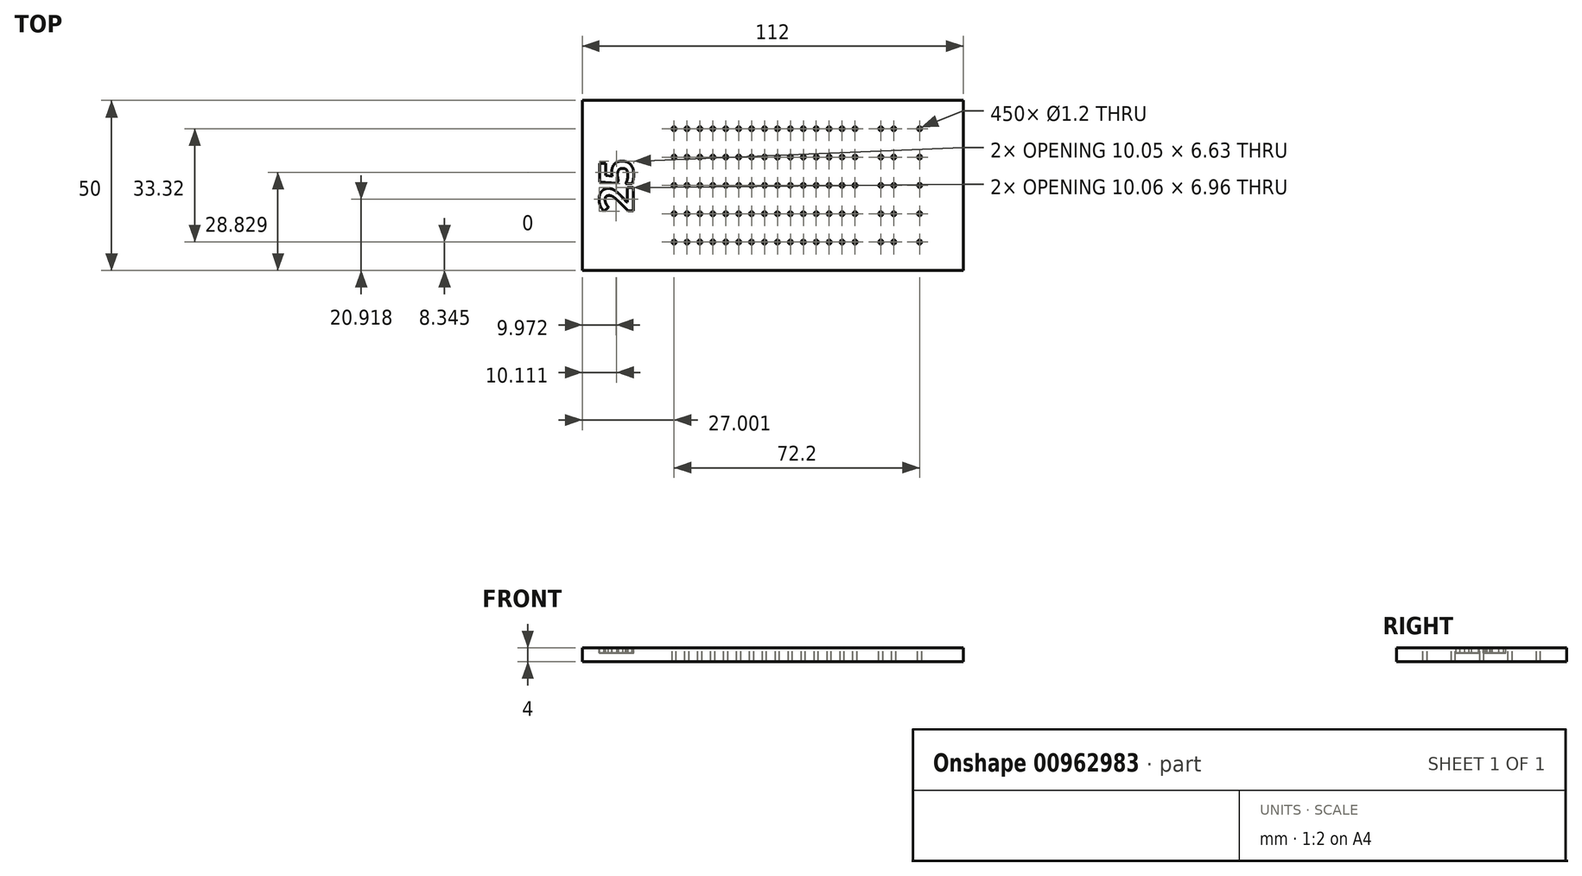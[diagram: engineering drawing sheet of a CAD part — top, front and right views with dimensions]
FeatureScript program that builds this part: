
annotation { "Feature Type Name" : "Feature", "Feature Type Description" : "" }
export const myFeature = defineFeature(function(context is Context, id is Id, definition is map)
    precondition{}
    {
        {
            var Q0;
            Q0=qCreatedBy(makeId("Top.planeOp"),FACE);
            var sketch = newSketch(context, id + "F0", { "sketchPlane" : qUnion([Q0])});
            skLineSegment(sketch, "E0.bottom", {"start": v(-43.16, 28.34) * mm, "end": v(68.84, 28.34) * mm});
            skLineSegment(sketch, "E0.top", {"start": v(-43.16, -21.66) * mm, "end": v(68.84, -21.66) * mm});
            skLineSegment(sketch, "E0.left", {"start": v(-43.16, 28.34) * mm, "end": v(-43.16, -21.66) * mm});
            skLineSegment(sketch, "E0.right", {"start": v(68.84, 28.34) * mm, "end": v(68.84, -21.66) * mm});
            skSolve(sketch);
        }
        {
            var Q0;
            Q0=makeQuery(id+"F0.imprint","IMPRINT",FACE,{"disambiguationData":[TD([[makeQuery(id+"F0.imprint","IMPRINT",EDGE,{"derivedFrom":sQuery(id+"F0.wireOp",EDGE,"E0.bottom")}),-1.0]])]});
            extrude(context, id + "F1", {"entities" : qUnion([Q0]), "depth" : 4 * mm, "offsetDistance" : 25 * mm});
        }
        {
            var Q0;
            Q0=makeQuery(id+"F1.opExtrude","CAP_FACE",FACE,{"disambiguationData":[OSD([sQuery(id+"F0.wireOp",EDGE,"E0.bottom"),sQuery(id+"F0.wireOp",EDGE,"E0.top"),sQuery(id+"F0.wireOp",EDGE,"E0.left"),sQuery(id+"F0.wireOp",EDGE,"E0.right")])],"isStart":false});
            var sketch = newSketch(context, id + "F2", { "sketchPlane" : qUnion([Q0])});
            skText(sketch, "E1", { "text": "25", "fontName": "OpenSans-Bold.ttf"});
            const initialGuessF2  = {"E1": [-0.02816, -0.00475, 0, 1, 0.01]};
            skSetInitialGuess(sketch, initialGuessF2);
            skSolve(sketch);
        }
        {
            var Q0;
            Q0=qSketchRegion(id+"F2",true);
            extrude(context, id + "F3", {"entities" : qUnion([Q0]), "operationType" : NewBodyOperationType.REMOVE, "oppositeDirection" : true, "depth" : 1.5 * mm, "offsetDistance" : 25 * mm});
        }
        {
            var Q0;
            {var subQ0=sQuery(id+"F0.wireOp",EDGE,"E0.left");var subQ1=sQuery(id+"F0.wireOp",EDGE,"E0.bottom");var subQ2=sQuery(id+"F0.wireOp",EDGE,"E0.right");var subQ3=sQuery(id+"F0.wireOp",EDGE,"E0.top");Q0=makeQuery(id+"F3.boolean.opBoolean","SPLIT",FACE,{"disambiguationData":[TD([makeQuery(id+"F1.opExtrude","SWEPT_FACE",FACE,{"disambiguationData":[OSD([subQ1])]})])],"derivedFrom":makeQuery(id+"F1.opExtrude","CAP_FACE",FACE,{"disambiguationData":[OSD([subQ1,subQ3,subQ0,subQ2])],"isStart":false})});}
            var sketch = newSketch(context, id + "F4", { "sketchPlane" : qUnion([Q0])});
            skCircle(sketch, "E2", {"center": v(-16.16, 20) * mm, "radius": 0.6 * mm});
            skCircle(sketch, "E3", {"center": v(-12.36, 20) * mm, "radius": 0.6 * mm});
            skCircle(sketch, "E4", {"center": v(-8.56, 20) * mm, "radius": 0.6 * mm});
            skCircle(sketch, "E5", {"center": v(-4.76, 20) * mm, "radius": 0.6 * mm});
            skCircle(sketch, "E6", {"center": v(-0.96, 20) * mm, "radius": 0.6 * mm});
            skCircle(sketch, "E7", {"center": v(2.84, 20) * mm, "radius": 0.6 * mm});
            skCircle(sketch, "E8", {"center": v(6.64, 20) * mm, "radius": 0.6 * mm});
            skCircle(sketch, "E9", {"center": v(10.44, 20) * mm, "radius": 0.6 * mm});
            skCircle(sketch, "E10", {"center": v(14.24, 20) * mm, "radius": 0.6 * mm});
            skCircle(sketch, "E11", {"center": v(18.04, 20) * mm, "radius": 0.6 * mm});
            skCircle(sketch, "E12", {"center": v(21.84, 20) * mm, "radius": 0.6 * mm});
            skCircle(sketch, "E13", {"center": v(25.64, 20) * mm, "radius": 0.6 * mm});
            skCircle(sketch, "E14", {"center": v(29.44, 20) * mm, "radius": 0.6 * mm});
            skCircle(sketch, "E15", {"center": v(33.24, 20) * mm, "radius": 0.6 * mm});
            skCircle(sketch, "E16", {"center": v(37.04, 20) * mm, "radius": 0.6 * mm});
            skCircle(sketch, "E17", {"center": v(44.64, 20) * mm, "radius": 0.6 * mm});
            skCircle(sketch, "E18", {"center": v(48.44, 20) * mm, "radius": 0.6 * mm});
            skCircle(sketch, "E19", {"center": v(56.04, 20) * mm, "radius": 0.6 * mm});
            skCircle(sketch, "E20", {"center": v(-16.16, 11.68) * mm, "radius": 0.6 * mm});
            skCircle(sketch, "E21", {"center": v(-12.36, 11.68) * mm, "radius": 0.6 * mm});
            skCircle(sketch, "E22", {"center": v(-8.56, 11.68) * mm, "radius": 0.6 * mm});
            skCircle(sketch, "E23", {"center": v(-4.76, 11.68) * mm, "radius": 0.6 * mm});
            skCircle(sketch, "E24", {"center": v(-0.96, 11.68) * mm, "radius": 0.6 * mm});
            skCircle(sketch, "E25", {"center": v(2.84, 11.68) * mm, "radius": 0.6 * mm});
            skCircle(sketch, "E26", {"center": v(6.64, 11.68) * mm, "radius": 0.6 * mm});
            skCircle(sketch, "E27", {"center": v(10.44, 11.68) * mm, "radius": 0.6 * mm});
            skCircle(sketch, "E28", {"center": v(14.24, 11.68) * mm, "radius": 0.6 * mm});
            skCircle(sketch, "E29", {"center": v(18.04, 11.68) * mm, "radius": 0.6 * mm});
            skCircle(sketch, "E30", {"center": v(21.84, 11.68) * mm, "radius": 0.6 * mm});
            skCircle(sketch, "E31", {"center": v(25.64, 11.68) * mm, "radius": 0.6 * mm});
            skCircle(sketch, "E32", {"center": v(29.44, 11.68) * mm, "radius": 0.6 * mm});
            skCircle(sketch, "E33", {"center": v(33.24, 11.68) * mm, "radius": 0.6 * mm});
            skCircle(sketch, "E34", {"center": v(37.04, 11.68) * mm, "radius": 0.6 * mm});
            skCircle(sketch, "E35", {"center": v(44.64, 11.68) * mm, "radius": 0.6 * mm});
            skCircle(sketch, "E36", {"center": v(48.44, 11.68) * mm, "radius": 0.6 * mm});
            skCircle(sketch, "E37", {"center": v(56.04, 11.68) * mm, "radius": 0.6 * mm});
            skCircle(sketch, "E38", {"center": v(-16.16, 3.35) * mm, "radius": 0.6 * mm});
            skCircle(sketch, "E39", {"center": v(-12.36, 3.35) * mm, "radius": 0.6 * mm});
            skCircle(sketch, "E40", {"center": v(-8.56, 3.35) * mm, "radius": 0.6 * mm});
            skCircle(sketch, "E41", {"center": v(-4.76, 3.35) * mm, "radius": 0.6 * mm});
            skCircle(sketch, "E42", {"center": v(-0.96, 3.35) * mm, "radius": 0.6 * mm});
            skCircle(sketch, "E43", {"center": v(2.84, 3.35) * mm, "radius": 0.6 * mm});
            skCircle(sketch, "E44", {"center": v(6.64, 3.35) * mm, "radius": 0.6 * mm});
            skCircle(sketch, "E45", {"center": v(10.44, 3.35) * mm, "radius": 0.6 * mm});
            skCircle(sketch, "E46", {"center": v(14.24, 3.35) * mm, "radius": 0.6 * mm});
            skCircle(sketch, "E47", {"center": v(18.04, 3.35) * mm, "radius": 0.6 * mm});
            skCircle(sketch, "E48", {"center": v(21.84, 3.35) * mm, "radius": 0.6 * mm});
            skCircle(sketch, "E49", {"center": v(25.64, 3.35) * mm, "radius": 0.6 * mm});
            skCircle(sketch, "E50", {"center": v(29.44, 3.35) * mm, "radius": 0.6 * mm});
            skCircle(sketch, "E51", {"center": v(33.24, 3.35) * mm, "radius": 0.6 * mm});
            skCircle(sketch, "E52", {"center": v(37.04, 3.35) * mm, "radius": 0.6 * mm});
            skCircle(sketch, "E53", {"center": v(44.64, 3.35) * mm, "radius": 0.6 * mm});
            skCircle(sketch, "E54", {"center": v(48.44, 3.35) * mm, "radius": 0.6 * mm});
            skCircle(sketch, "E55", {"center": v(56.04, 3.35) * mm, "radius": 0.6 * mm});
            skCircle(sketch, "E56", {"center": v(-16.16, -4.98) * mm, "radius": 0.6 * mm});
            skCircle(sketch, "E57", {"center": v(-12.36, -4.98) * mm, "radius": 0.6 * mm});
            skCircle(sketch, "E58", {"center": v(-8.56, -4.98) * mm, "radius": 0.6 * mm});
            skCircle(sketch, "E59", {"center": v(-4.76, -4.98) * mm, "radius": 0.6 * mm});
            skCircle(sketch, "E60", {"center": v(-0.96, -4.98) * mm, "radius": 0.6 * mm});
            skCircle(sketch, "E61", {"center": v(2.84, -4.98) * mm, "radius": 0.6 * mm});
            skCircle(sketch, "E62", {"center": v(6.64, -4.98) * mm, "radius": 0.6 * mm});
            skCircle(sketch, "E63", {"center": v(10.44, -4.98) * mm, "radius": 0.6 * mm});
            skCircle(sketch, "E64", {"center": v(14.24, -4.98) * mm, "radius": 0.6 * mm});
            skCircle(sketch, "E65", {"center": v(18.04, -4.98) * mm, "radius": 0.6 * mm});
            skCircle(sketch, "E66", {"center": v(21.84, -4.98) * mm, "radius": 0.6 * mm});
            skCircle(sketch, "E67", {"center": v(25.64, -4.98) * mm, "radius": 0.6 * mm});
            skCircle(sketch, "E68", {"center": v(29.44, -4.98) * mm, "radius": 0.6 * mm});
            skCircle(sketch, "E69", {"center": v(33.24, -4.98) * mm, "radius": 0.6 * mm});
            skCircle(sketch, "E70", {"center": v(37.04, -4.98) * mm, "radius": 0.6 * mm});
            skCircle(sketch, "E71", {"center": v(44.64, -4.98) * mm, "radius": 0.6 * mm});
            skCircle(sketch, "E72", {"center": v(48.44, -4.98) * mm, "radius": 0.6 * mm});
            skCircle(sketch, "E73", {"center": v(56.04, -4.98) * mm, "radius": 0.6 * mm});
            skCircle(sketch, "E74", {"center": v(-16.16, -13.31) * mm, "radius": 0.6 * mm});
            skCircle(sketch, "E75", {"center": v(-12.36, -13.31) * mm, "radius": 0.6 * mm});
            skCircle(sketch, "E76", {"center": v(-8.56, -13.31) * mm, "radius": 0.6 * mm});
            skCircle(sketch, "E77", {"center": v(-4.76, -13.31) * mm, "radius": 0.6 * mm});
            skCircle(sketch, "E78", {"center": v(-0.96, -13.31) * mm, "radius": 0.6 * mm});
            skCircle(sketch, "E79", {"center": v(2.84, -13.31) * mm, "radius": 0.6 * mm});
            skCircle(sketch, "E80", {"center": v(6.64, -13.31) * mm, "radius": 0.6 * mm});
            skCircle(sketch, "E81", {"center": v(10.44, -13.31) * mm, "radius": 0.6 * mm});
            skCircle(sketch, "E82", {"center": v(14.24, -13.31) * mm, "radius": 0.6 * mm});
            skCircle(sketch, "E83", {"center": v(18.04, -13.31) * mm, "radius": 0.6 * mm});
            skCircle(sketch, "E84", {"center": v(21.84, -13.31) * mm, "radius": 0.6 * mm});
            skCircle(sketch, "E85", {"center": v(25.64, -13.31) * mm, "radius": 0.6 * mm});
            skCircle(sketch, "E86", {"center": v(29.44, -13.31) * mm, "radius": 0.6 * mm});
            skCircle(sketch, "E87", {"center": v(33.24, -13.31) * mm, "radius": 0.6 * mm});
            skCircle(sketch, "E88", {"center": v(37.04, -13.31) * mm, "radius": 0.6 * mm});
            skCircle(sketch, "E89", {"center": v(44.64, -13.31) * mm, "radius": 0.6 * mm});
            skCircle(sketch, "E90", {"center": v(48.44, -13.31) * mm, "radius": 0.6 * mm});
            skCircle(sketch, "E91", {"center": v(56.04, -13.31) * mm, "radius": 0.6 * mm});
            skSolve(sketch);
        }
        {
            var Q0;
            Q0 = qSketchRegion(id + "F4", true);
            extrude(context, id + "F5", {"entities" : qUnion([Q0]), "operationType" : NewBodyOperationType.REMOVE, "endBound" : BoundingType.UP_TO_NEXT, "oppositeDirection" : true, "depth" : 25 * mm, "offsetDistance" : 25 * mm});
        }
    });
